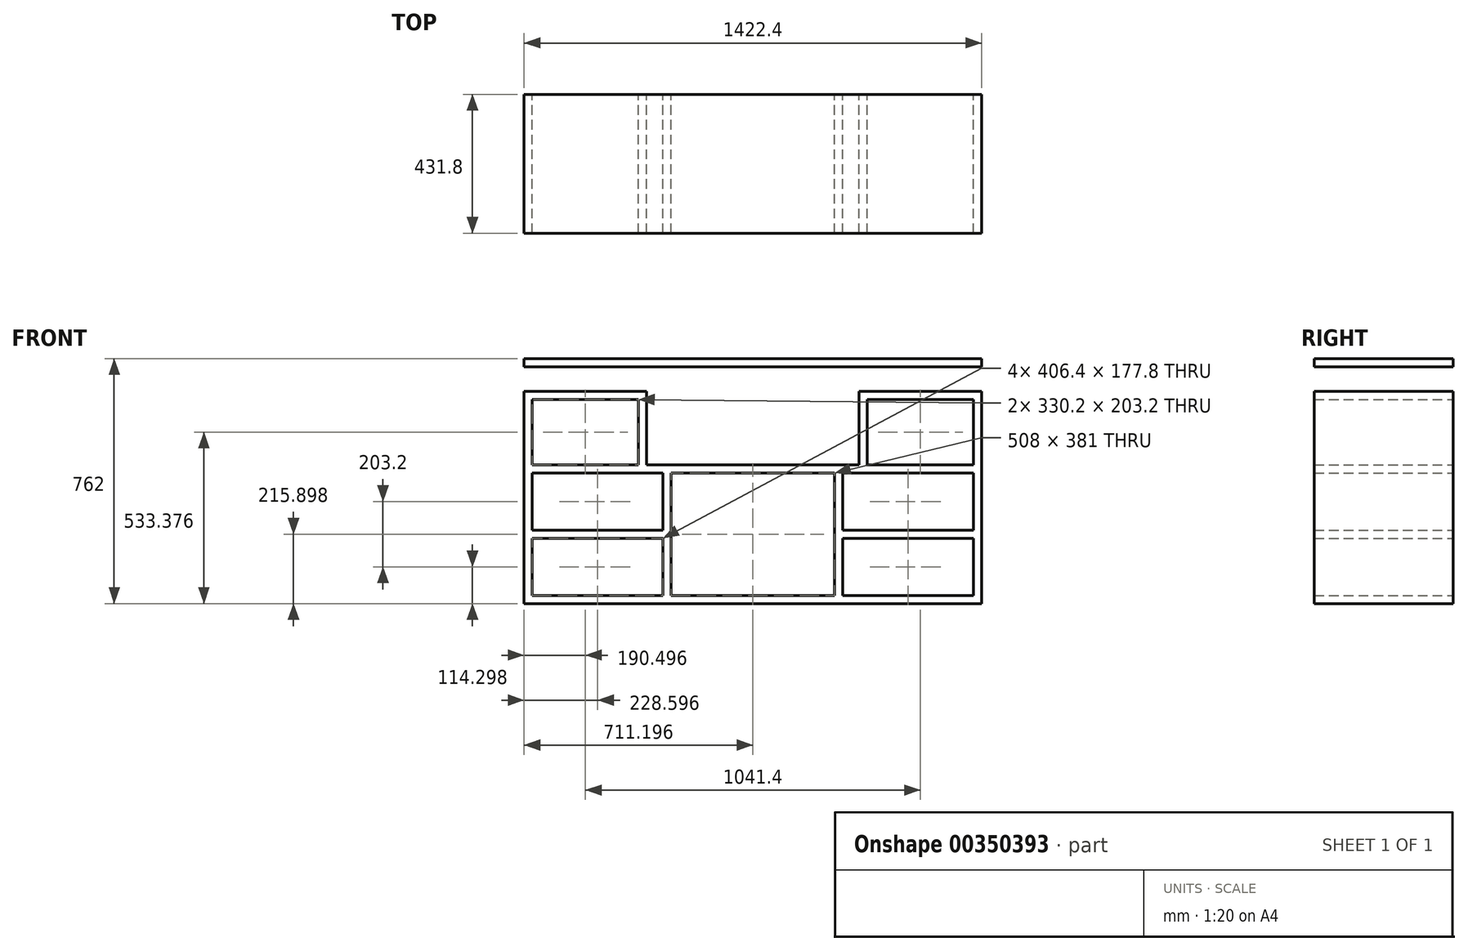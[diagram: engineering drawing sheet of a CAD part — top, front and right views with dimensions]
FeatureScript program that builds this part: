
annotation { "Feature Type Name" : "Feature", "Feature Type Description" : "" }
export const myFeature = defineFeature(function(context is Context, id is Id, definition is map)
    precondition{}
    {
        {
            var Q0;
            Q0=qCreatedBy(makeId("Front.planeOp"),FACE);
            var sketch = newSketch(context, id + "F0", { "sketchPlane" : qUnion([Q0])});
            skLineSegment(sketch, "E0.top", {"start": v(-521.91, -350.05) * mm, "end": v(900.49, -350.05) * mm});
            skLineSegment(sketch, "E0.left", {"start": v(-521.91, 411.95) * mm, "end": v(-521.91, 386.55) * mm});
            skLineSegment(sketch, "E0.right", {"start": v(900.49, 411.95) * mm, "end": v(900.49, 386.55) * mm});
            skLineSegment(sketch, "E1", {"start": v(900.49, -324.65) * mm, "end": v(900.49, -350.05) * mm});
            skLineSegment(sketch, "E2", {"start": v(-521.91, -324.65) * mm, "end": v(-521.91, -350.05) * mm});
            skLineSegment(sketch, "E3", {"start": v(-521.91, 310.33) * mm, "end": v(-521.91, 284.93) * mm});
            skLineSegment(sketch, "E4", {"start": v(900.49, 310.35) * mm, "end": v(900.49, 284.95) * mm});
            skLineSegment(sketch, "E5", {"start": v(-521.91, 411.95) * mm, "end": v(900.49, 411.95) * mm});
            skLineSegment(sketch, "E6", {"start": v(-521.91, 386.55) * mm, "end": v(900.49, 386.55) * mm});
            skLineSegment(sketch, "E7", {"start": v(-521.91, 310.33) * mm, "end": v(-140.91, 310.33) * mm});
            skLineSegment(sketch, "E8", {"start": v(-521.91, 284.93) * mm, "end": v(-521.91, 81.72) * mm});
            skLineSegment(sketch, "E9", {"start": v(900.49, 284.95) * mm, "end": v(900.49, 81.75) * mm});
            skLineSegment(sketch, "E10", {"start": v(519.49, 310.35) * mm, "end": v(900.49, 310.35) * mm});
            skLineSegment(sketch, "E11", {"start": v(-140.91, 310.33) * mm, "end": v(-140.91, 284.93) * mm});
            skLineSegment(sketch, "E12", {"start": v(519.49, 310.35) * mm, "end": v(519.49, 284.95) * mm});
            skLineSegment(sketch, "E13", {"start": v(-140.91, 284.93) * mm, "end": v(-140.91, 81.77) * mm});
            skLineSegment(sketch, "E14", {"start": v(519.49, 284.95) * mm, "end": v(519.49, 81.77) * mm});
            skLineSegment(sketch, "E15", {"start": v(-521.91, 284.93) * mm, "end": v(-496.51, 284.93) * mm});
            skLineSegment(sketch, "E16", {"start": v(519.49, 284.95) * mm, "end": v(544.89, 284.95) * mm});
            skLineSegment(sketch, "E17", {"start": v(-140.91, 81.77) * mm, "end": v(519.49, 81.77) * mm});
            skLineSegment(sketch, "E18", {"start": v(-521.91, 81.72) * mm, "end": v(-521.91, 56.35) * mm});
            skLineSegment(sketch, "E19", {"start": v(900.49, 81.75) * mm, "end": v(900.49, 56.35) * mm});
            skLineSegment(sketch, "E20", {"start": v(-496.51, 284.93) * mm, "end": v(-166.31, 284.93) * mm});
            skLineSegment(sketch, "E21", {"start": v(-166.31, 284.93) * mm, "end": v(-140.91, 284.93) * mm});
            skLineSegment(sketch, "E22", {"start": v(544.89, 284.95) * mm, "end": v(875.09, 284.95) * mm});
            skLineSegment(sketch, "E23", {"start": v(875.09, 284.95) * mm, "end": v(900.49, 284.95) * mm});
            skLineSegment(sketch, "E24", {"start": v(-521.91, 81.72) * mm, "end": v(-496.51, 81.73) * mm});
            skLineSegment(sketch, "E25", {"start": v(519.49, 81.77) * mm, "end": v(544.89, 81.77) * mm});
            skLineSegment(sketch, "E26", {"start": v(-521.91, 56.35) * mm, "end": v(-521.91, -324.65) * mm});
            skLineSegment(sketch, "E27", {"start": v(900.49, 56.35) * mm, "end": v(900.49, -324.65) * mm});
            skLineSegment(sketch, "E28", {"start": v(-521.91, 56.35) * mm, "end": v(-496.51, 56.35) * mm});
            skLineSegment(sketch, "E29", {"start": v(-166.31, 81.77) * mm, "end": v(-140.91, 81.77) * mm});
            skLineSegment(sketch, "E30", {"start": v(-496.51, 81.73) * mm, "end": v(-166.31, 81.77) * mm});
            skLineSegment(sketch, "E31", {"start": v(544.89, 81.77) * mm, "end": v(875.09, 81.75) * mm});
            skLineSegment(sketch, "E32", {"start": v(875.09, 81.75) * mm, "end": v(900.49, 81.75) * mm});
            skLineSegment(sketch, "E33", {"start": v(875.09, 56.35) * mm, "end": v(900.49, 56.35) * mm});
            skLineSegment(sketch, "E34", {"start": v(468.69, 56.35) * mm, "end": v(875.09, 56.35) * mm});
            skLineSegment(sketch, "E35", {"start": v(443.29, 56.35) * mm, "end": v(468.69, 56.35) * mm});
            skLineSegment(sketch, "E36", {"start": v(-64.71, 56.35) * mm, "end": v(443.29, 56.35) * mm});
            skLineSegment(sketch, "E37", {"start": v(-90.11, 56.35) * mm, "end": v(-64.71, 56.35) * mm});
            skLineSegment(sketch, "E38", {"start": v(-496.51, 56.35) * mm, "end": v(-90.11, 56.35) * mm});
            skLineSegment(sketch, "E39", {"start": v(-496.51, 284.93) * mm, "end": v(-496.51, 81.73) * mm});
            skLineSegment(sketch, "E40", {"start": v(-166.31, 284.93) * mm, "end": v(-166.31, 81.77) * mm});
            skLineSegment(sketch, "E41", {"start": v(544.89, 284.95) * mm, "end": v(544.89, 81.77) * mm});
            skLineSegment(sketch, "E42", {"start": v(875.09, 284.95) * mm, "end": v(875.09, 81.75) * mm});
            skLineSegment(sketch, "E43", {"start": v(-521.91, -324.65) * mm, "end": v(-496.51, -324.65) * mm});
            skLineSegment(sketch, "E44", {"start": v(-64.71, -324.65) * mm, "end": v(443.29, -324.65) * mm});
            skLineSegment(sketch, "E45", {"start": v(-90.11, -324.65) * mm, "end": v(-64.71, -324.65) * mm});
            skLineSegment(sketch, "E46", {"start": v(443.29, -324.65) * mm, "end": v(468.69, -324.65) * mm});
            skLineSegment(sketch, "E47", {"start": v(468.69, -324.65) * mm, "end": v(875.09, -324.65) * mm});
            skLineSegment(sketch, "E48", {"start": v(-90.11, 56.35) * mm, "end": v(-90.11, -121.45) * mm});
            skLineSegment(sketch, "E49", {"start": v(-64.71, -324.65) * mm, "end": v(-64.71, 56.35) * mm});
            skLineSegment(sketch, "E50", {"start": v(443.29, 56.35) * mm, "end": v(443.29, -324.65) * mm});
            skLineSegment(sketch, "E51", {"start": v(468.69, -324.65) * mm, "end": v(468.69, -146.85) * mm});
            skLineSegment(sketch, "E52", {"start": v(-496.51, -324.65) * mm, "end": v(-90.11, -324.65) * mm});
            skLineSegment(sketch, "E53", {"start": v(875.09, -324.65) * mm, "end": v(900.49, -324.65) * mm});
            skLineSegment(sketch, "E54", {"start": v(-496.51, 56.35) * mm, "end": v(-496.51, -121.45) * mm});
            skLineSegment(sketch, "E55", {"start": v(875.09, -324.65) * mm, "end": v(875.09, -146.85) * mm});
            skLineSegment(sketch, "E56", {"start": v(-90.11, -121.45) * mm, "end": v(-90.11, -146.85) * mm});
            skLineSegment(sketch, "E57", {"start": v(-90.11, -146.85) * mm, "end": v(-90.11, -324.65) * mm});
            skLineSegment(sketch, "E58", {"start": v(-496.51, -121.45) * mm, "end": v(-496.51, -146.85) * mm});
            skLineSegment(sketch, "E59", {"start": v(-496.51, -146.85) * mm, "end": v(-496.51, -324.65) * mm});
            skLineSegment(sketch, "E60", {"start": v(468.69, -121.45) * mm, "end": v(468.69, 56.35) * mm});
            skLineSegment(sketch, "E61", {"start": v(468.69, -146.85) * mm, "end": v(468.69, -121.45) * mm});
            skLineSegment(sketch, "E62", {"start": v(875.09, -146.85) * mm, "end": v(875.09, -121.45) * mm});
            skLineSegment(sketch, "E63", {"start": v(875.09, -121.45) * mm, "end": v(875.09, 56.35) * mm});
            skLineSegment(sketch, "E64", {"start": v(468.69, -121.45) * mm, "end": v(875.09, -121.45) * mm});
            skLineSegment(sketch, "E65", {"start": v(468.69, -146.85) * mm, "end": v(875.09, -146.85) * mm});
            skLineSegment(sketch, "E66", {"start": v(-496.51, -121.45) * mm, "end": v(-90.11, -121.45) * mm});
            skLineSegment(sketch, "E67", {"start": v(-496.51, -146.85) * mm, "end": v(-90.11, -146.85) * mm});
            skSolve(sketch);
        }
        {
            var Q0;
            Q0=makeQuery(id+"F0.imprint","IMPRINT",FACE,{"disambiguationData":[TD([[makeQuery(id+"F0.imprint","IMPRINT",EDGE,{"derivedFrom":sQuery(id+"F0.wireOp",EDGE,"E17")}),-1.0]])]});
            var Q1;
            Q1=makeQuery(id+"F0.imprint","IMPRINT",FACE,{"disambiguationData":[TD([[makeQuery(id+"F0.imprint","IMPRINT",EDGE,{"derivedFrom":sQuery(id+"F0.wireOp",EDGE,"E3")}),1.0]])]});
            var Q2;
            Q2=makeQuery(id+"F0.imprint","IMPRINT",FACE,{"disambiguationData":[TD([[makeQuery(id+"F0.imprint","IMPRINT",EDGE,{"derivedFrom":sQuery(id+"F0.wireOp",EDGE,"E4")}),-1.0]])]});
            var Q3;
            Q3=makeQuery(id+"F0.imprint","IMPRINT",FACE,{"disambiguationData":[TD([[makeQuery(id+"F0.imprint","IMPRINT",EDGE,{"derivedFrom":sQuery(id+"F0.wireOp",EDGE,"E8")}),1.0]])]});
            var Q4;
            Q4=makeQuery(id+"F0.imprint","IMPRINT",FACE,{"disambiguationData":[TD([[makeQuery(id+"F0.imprint","IMPRINT",EDGE,{"derivedFrom":sQuery(id+"F0.wireOp",EDGE,"E9")}),-1.0]])]});
            var Q5;
            Q5=makeQuery(id+"F0.imprint","IMPRINT",FACE,{"disambiguationData":[TD([[makeQuery(id+"F0.imprint","IMPRINT",EDGE,{"derivedFrom":sQuery(id+"F0.wireOp",EDGE,"E13")}),-1.0]])]});
            var Q6;
            Q6=makeQuery(id+"F0.imprint","IMPRINT",FACE,{"disambiguationData":[TD([[makeQuery(id+"F0.imprint","IMPRINT",EDGE,{"derivedFrom":sQuery(id+"F0.wireOp",EDGE,"E14")}),1.0]])]});
            var Q7;
            Q7=makeQuery(id+"F0.imprint","IMPRINT",FACE,{"disambiguationData":[TD([[makeQuery(id+"F0.imprint","IMPRINT",EDGE,{"derivedFrom":sQuery(id+"F0.wireOp",EDGE,"E27")}),-1.0]])]});
            var Q8;
            Q8=makeQuery(id+"F0.imprint","IMPRINT",FACE,{"disambiguationData":[TD([[makeQuery(id+"F0.imprint","IMPRINT",EDGE,{"derivedFrom":sQuery(id+"F0.wireOp",EDGE,"E0.top")}),1.0]])]});
            var Q9;
            Q9=makeQuery(id+"F0.imprint","IMPRINT",FACE,{"disambiguationData":[TD([[makeQuery(id+"F0.imprint","IMPRINT",EDGE,{"derivedFrom":sQuery(id+"F0.wireOp",EDGE,"E35")}),-1.0]])]});
            var Q10;
            Q10=makeQuery(id+"F0.imprint","IMPRINT",FACE,{"disambiguationData":[TD([[makeQuery(id+"F0.imprint","IMPRINT",EDGE,{"derivedFrom":sQuery(id+"F0.wireOp",EDGE,"E61")}),-1.0]])]});
            var Q11;
            Q11=makeQuery(id+"F0.imprint","IMPRINT",FACE,{"disambiguationData":[TD([[makeQuery(id+"F0.imprint","IMPRINT",EDGE,{"derivedFrom":sQuery(id+"F0.wireOp",EDGE,"E26")}),1.0]])]});
            var Q12;
            Q12=makeQuery(id+"F0.imprint","IMPRINT",FACE,{"disambiguationData":[TD([[makeQuery(id+"F0.imprint","IMPRINT",EDGE,{"derivedFrom":sQuery(id+"F0.wireOp",EDGE,"E56")}),-1.0]])]});
            var Q13;
            Q13=makeQuery(id+"F0.imprint","IMPRINT",FACE,{"disambiguationData":[TD([[makeQuery(id+"F0.imprint","IMPRINT",EDGE,{"derivedFrom":sQuery(id+"F0.wireOp",EDGE,"E0.left")}),1.0]])]});
            var Q14;
            Q14=makeQuery(id+"F0.imprint","IMPRINT",FACE,{"disambiguationData":[TD([[makeQuery(id+"F0.imprint","IMPRINT",EDGE,{"derivedFrom":sQuery(id+"F0.wireOp",EDGE,"E37")}),-1.0]])]});
            extrude(context, id + "F1", {"entities" : qUnion([Q0, Q1, Q2, Q3, Q4, Q5, Q6, Q7, Q8, Q9, Q10, Q11, Q12, Q13, Q14]), "depth" : 431.8 * mm});
        }
    });
